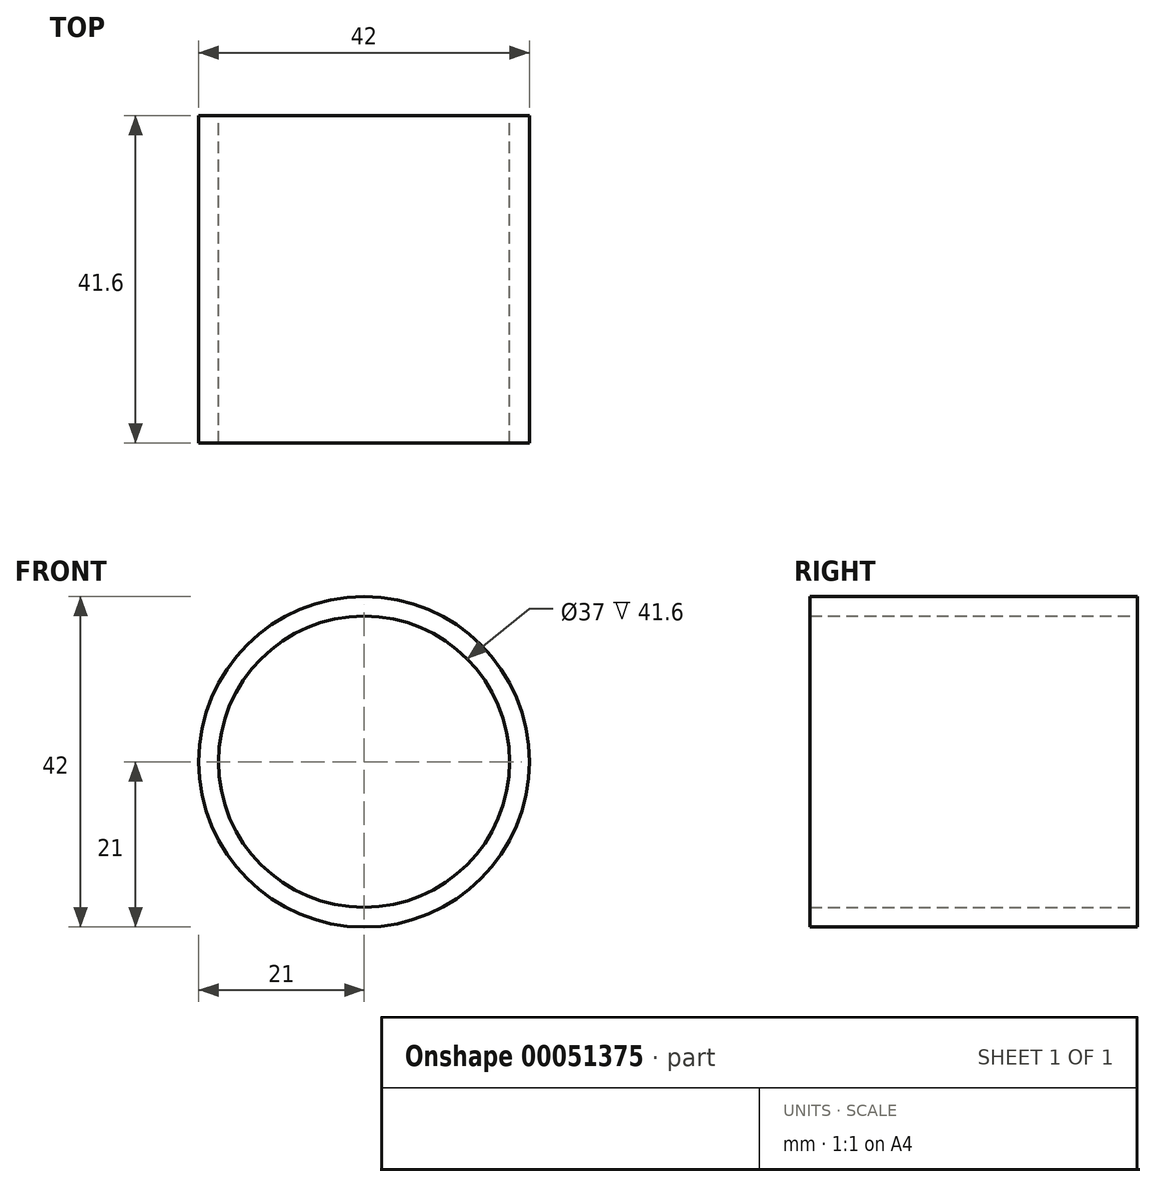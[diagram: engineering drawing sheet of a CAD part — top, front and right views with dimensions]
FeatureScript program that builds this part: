
annotation { "Feature Type Name" : "Feature", "Feature Type Description" : "" }
export const myFeature = defineFeature(function(context is Context, id is Id, definition is map)
    precondition{}
    {
        {
            var Q0;
            Q0=qCreatedBy(makeId("Front.planeOp"),FACE);
            var sketch = newSketch(context, id + "F0", { "sketchPlane" : qUnion([Q0])});
            skCircle(sketch, "E0", {"center": v(0, 0) * mm, "radius": 21 * mm});
            skCircle(sketch, "E1", {"center": v(0, 0) * mm, "radius": 18.5 * mm});
            skSolve(sketch);
        }
        {
            var Q0;
            Q0=qSketchRegion(id+"F0",true);
            extrude(context, id + "F1", {"entities" : qUnion([Q0]), "depth" : 20.8 * mm, "hasSecondDirection" : true, "secondDirectionOppositeDirection" : true, "secondDirectionDepth" : 20.8 * mm});
        }
    });
